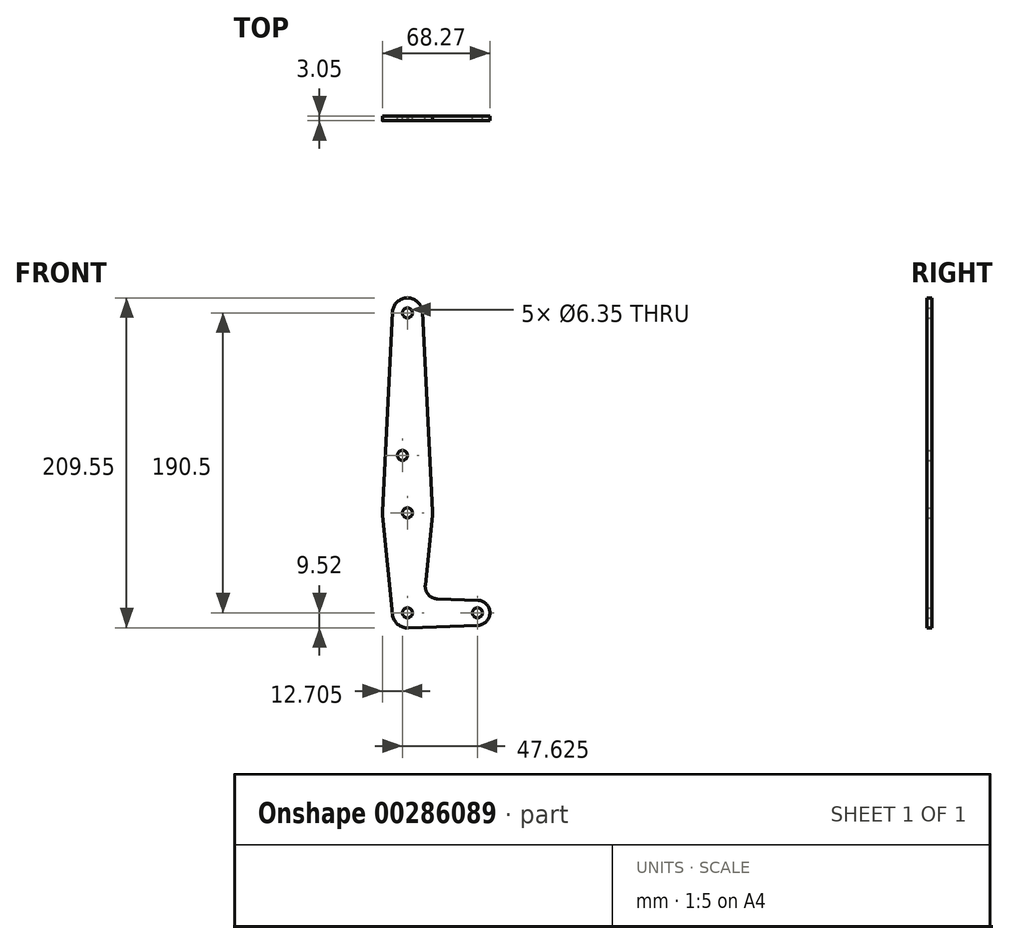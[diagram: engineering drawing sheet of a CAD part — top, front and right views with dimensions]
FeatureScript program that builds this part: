
annotation { "Feature Type Name" : "Feature", "Feature Type Description" : "" }
export const myFeature = defineFeature(function(context is Context, id is Id, definition is map)
    precondition{}
    {
        {
            var Q0;
            Q0=qCreatedBy(makeId("Front.planeOp"),FACE);
            var sketch = newSketch(context, id + "F0", { "sketchPlane" : qUnion([Q0])});
            skCircle(sketch, "E0", {"center": v(0, 127) * mm, "radius": 9.52 * mm});
            skCircle(sketch, "E1", {"center": v(0, 0) * mm, "radius": 15.88 * mm});
            skCircle(sketch, "E2", {"center": v(0, -63.5) * mm, "radius": 9.52 * mm});
            skCircle(sketch, "E3", {"center": v(44.45, -63.5) * mm, "radius": 7.94 * mm});
            skLineSegment(sketch, "E4", {"start": v(0, 127) * mm, "end": v(0, -63.5) * mm, "construction": true});
            skLineSegment(sketch, "E5", {"start": v(0, -63.5) * mm, "end": v(44.45, -63.5) * mm, "construction": true});
            skLineSegment(sketch, "E6", {"start": v(-15.86, 0.8) * mm, "end": v(-9.51, 127.48) * mm});
            skLineSegment(sketch, "E7", {"start": v(15.86, 0.8) * mm, "end": v(9.51, 127.48) * mm});
            skLineSegment(sketch, "E8", {"start": v(-15.8, -1.59) * mm, "end": v(-9.48, -64.45) * mm});
            skLineSegment(sketch, "E9", {"start": v(15.8, -1.59) * mm, "end": v(11.34, -45.9) * mm});
            skLineSegment(sketch, "E10", {"start": v(0, -73.02) * mm, "end": v(44.73, -71.43) * mm});
            skLineSegment(sketch, "E11", {"start": v(44.73, -55.57) * mm, "end": v(18.97, -54.65) * mm});
            skCircle(sketch, "E12", {"center": v(0, 127) * mm, "radius": 3.18 * mm});
            skCircle(sketch, "E13", {"center": v(-3.17, 36.53) * mm, "radius": 3.18 * mm});
            skCircle(sketch, "E14", {"center": v(0, 0) * mm, "radius": 3.18 * mm});
            skCircle(sketch, "E15", {"center": v(0, -63.5) * mm, "radius": 3.18 * mm});
            skCircle(sketch, "E16", {"center": v(44.45, -63.5) * mm, "radius": 3.18 * mm});
            skArc(sketch, "E17.filletArc", {"start": v(11.34, -45.9) * mm, "mid": v(13.26, -51.93) * mm, "end": v(18.97, -54.65) * mm});
            skSolve(sketch);
        }
        {
            var Q0;
            Q0 = qSketchRegion(id + "F0", true);
            extrude(context, id + "F1", {"entities" : qUnion([Q0]), "depth" : 3.05 * mm});
        }
    });
